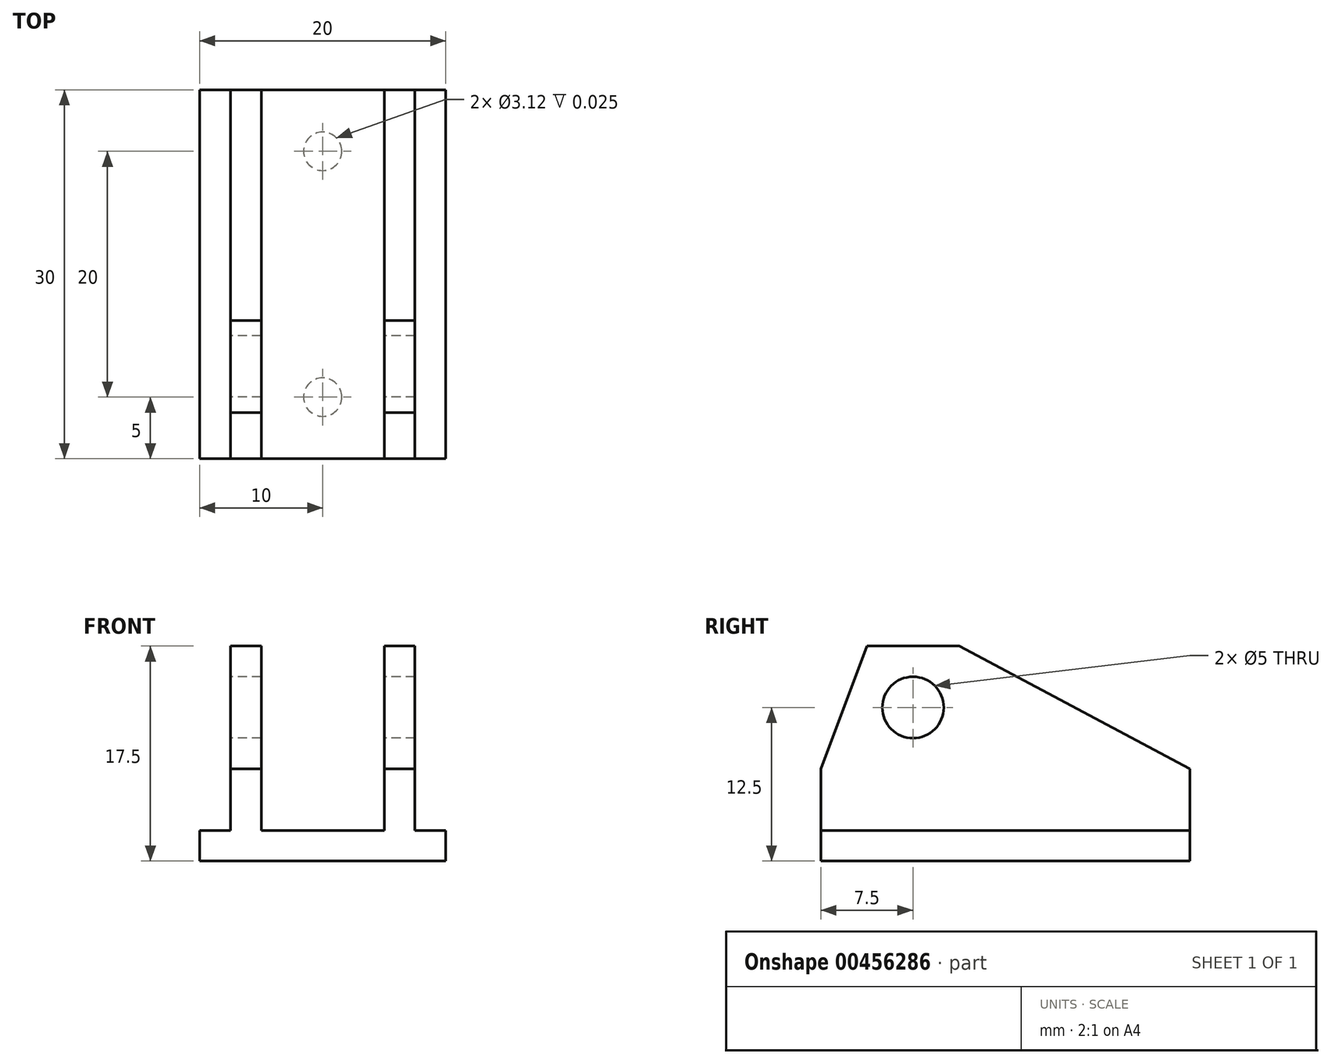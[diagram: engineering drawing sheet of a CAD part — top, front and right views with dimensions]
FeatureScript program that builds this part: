
annotation { "Feature Type Name" : "Feature", "Feature Type Description" : "" }
export const myFeature = defineFeature(function(context is Context, id is Id, definition is map)
    precondition{}
    {
        {
            var Q0;
            Q0=qCreatedBy(makeId("Right.planeOp"),FACE);
            var sketch = newSketch(context, id + "F0", { "sketchPlane" : qUnion([Q0])});
            skLineSegment(sketch, "E0.bottom", {"start": v(0, 0) * mm, "end": v(30, 0) * mm});
            skLineSegment(sketch, "E0.top", {"start": v(0, 2.5) * mm, "end": v(30, 2.5) * mm});
            skLineSegment(sketch, "E0.left", {"start": v(0, 0) * mm, "end": v(0, 2.5) * mm});
            skLineSegment(sketch, "E0.right", {"start": v(30, 0) * mm, "end": v(30, 2.5) * mm});
            skLineSegment(sketch, "E1", {"start": v(0, 2.5) * mm, "end": v(0, 7.5) * mm});
            skLineSegment(sketch, "E2", {"start": v(0, 7.5) * mm, "end": v(3.75, 17.5) * mm});
            skLineSegment(sketch, "E3", {"start": v(3.75, 17.5) * mm, "end": v(11.25, 17.5) * mm});
            skLineSegment(sketch, "E4", {"start": v(11.25, 17.5) * mm, "end": v(30, 7.5) * mm});
            skLineSegment(sketch, "E5", {"start": v(30, 7.5) * mm, "end": v(30, 2.5) * mm});
            skCircle(sketch, "E6", {"center": v(7.5, 12.5) * mm, "radius": 2.5 * mm});
            skSolve(sketch);
        }
        {
            var Q0;
            Q0=makeQuery(id+"F0.imprint","IMPRINT",FACE,{"disambiguationData":[TD([[makeQuery(id+"F0.imprint","IMPRINT",EDGE,{"derivedFrom":sQuery(id+"F0.wireOp",EDGE,"E0.bottom")}),1.0]])]});
            extrude(context, id + "F1", {"entities" : qUnion([Q0]), "endBound" : BoundingType.SYMMETRIC, "depth" : 20 * mm, "offsetDistance" : 25 * mm});
        }
        {
            var Q0;
            Q0=makeQuery(id+"F0.imprint","IMPRINT",FACE,{"disambiguationData":[TD([[makeQuery(id+"F0.imprint","IMPRINT",EDGE,{"derivedFrom":sQuery(id+"F0.wireOp",EDGE,"E0.top")}),1.0]])]});
            extrude(context, id + "F2", {"entities" : qUnion([Q0]), "operationType" : NewBodyOperationType.ADD, "endBound" : BoundingType.SYMMETRIC, "depth" : 15 * mm, "offsetDistance" : 25 * mm});
        }
        {
            var Q0;
            Q0=makeQuery(id+"F0.imprint","IMPRINT",FACE,{"disambiguationData":[TD([[makeQuery(id+"F0.imprint","IMPRINT",EDGE,{"derivedFrom":sQuery(id+"F0.wireOp",EDGE,"E0.top")}),1.0]])]});
            extrude(context, id + "F3", {"entities" : qUnion([Q0]), "operationType" : NewBodyOperationType.REMOVE, "endBound" : BoundingType.SYMMETRIC, "oppositeDirection" : true, "depth" : 10 * mm, "offsetDistance" : 25 * mm});
        }
        {
            var Q0;
            Q0=qCreatedBy(makeId("Top.planeOp"),FACE);
            var sketch = newSketch(context, id + "F4", { "sketchPlane" : qUnion([Q0])});
            skCircle(sketch, "E7", {"center": v(0, 5) * mm, "radius": 1.56 * mm});
            skCircle(sketch, "E8", {"center": v(0, 25) * mm, "radius": 1.56 * mm});
            skSolve(sketch);
        }
        {
            var Q0;
            Q0 = qSketchRegion(id + "F4", true);
            extrude(context, id + "F5", {"entities" : qUnion([Q0]), "operationType" : NewBodyOperationType.REMOVE, "depth" : 1 / 40 * mm, "offsetDistance" : 25 * mm});
        }
    });
